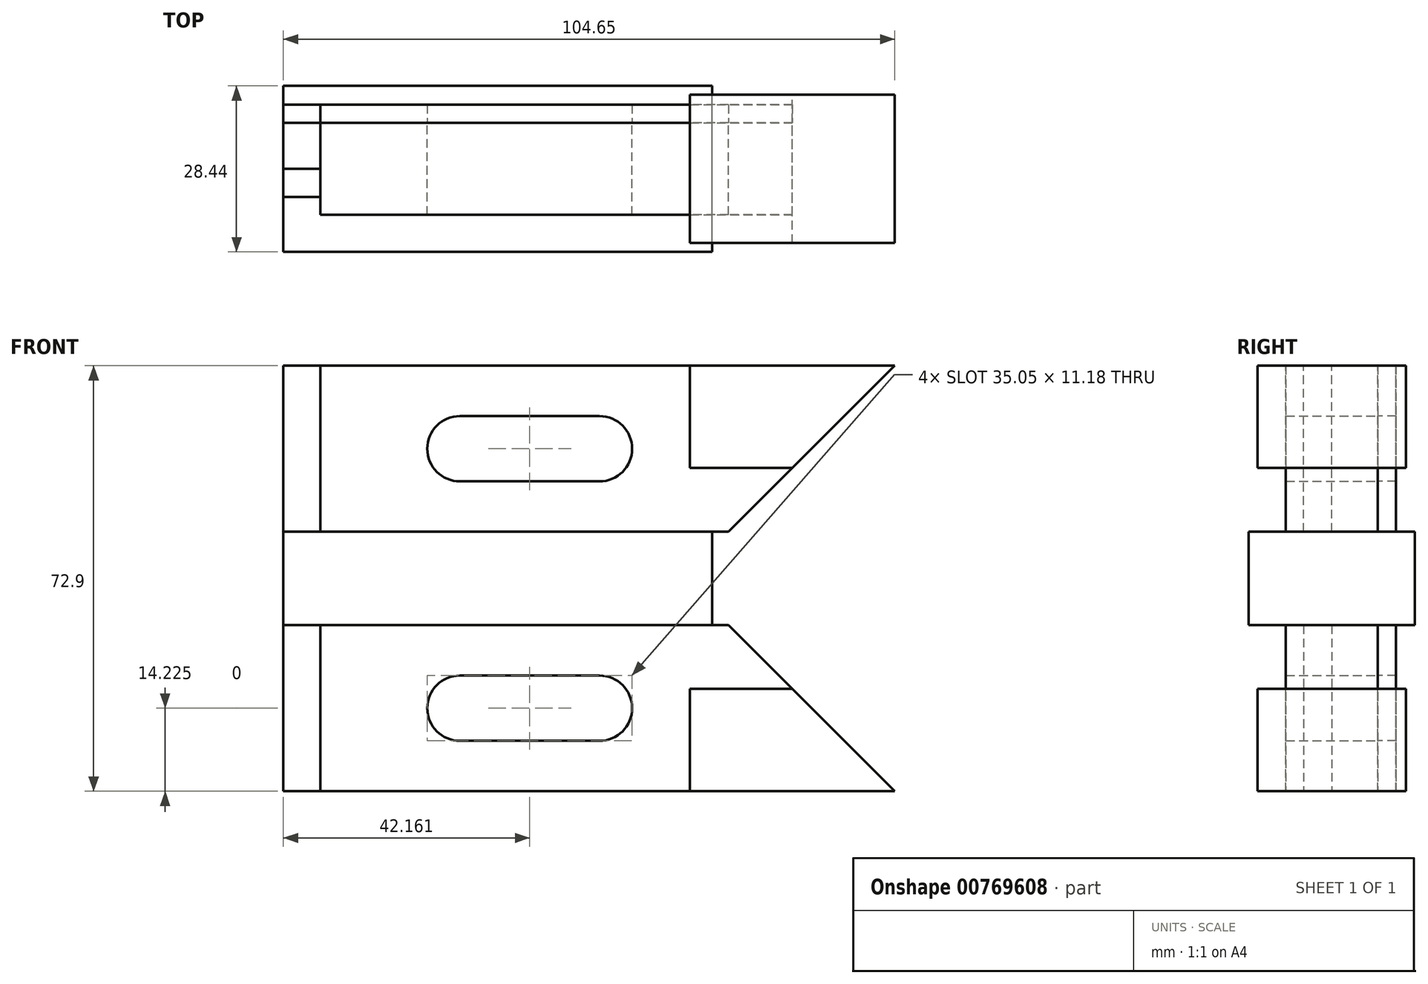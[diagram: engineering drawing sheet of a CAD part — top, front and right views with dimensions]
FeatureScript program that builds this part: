
annotation { "Feature Type Name" : "Feature", "Feature Type Description" : "" }
export const myFeature = defineFeature(function(context is Context, id is Id, definition is map)
    precondition{}
    {
        {
            var Q0;
            Q0=qCreatedBy(makeId("Front.planeOp"),FACE);
            var sketch = newSketch(context, id + "F0", { "sketchPlane" : qUnion([Q0])});
            skLineSegment(sketch, "E0.bottom", {"start": v(36.7, 8) * mm, "end": v(-36.7, 8) * mm});
            skLineSegment(sketch, "E0.top", {"start": v(36.7, -8) * mm, "end": v(-36.7, -8) * mm});
            skLineSegment(sketch, "E0.left", {"start": v(36.7, 8) * mm, "end": v(36.7, -8) * mm});
            skLineSegment(sketch, "E0.right", {"start": v(-36.7, 8) * mm, "end": v(-36.7, -8) * mm});
            skPoint(sketch, "E0.middle", {"position": v(0, 0) * mm});
            skLineSegment(sketch, "E1.bottom", {"start": v(-36.7, 8) * mm, "end": v(36.7, 8) * mm});
            skLineSegment(sketch, "E1.top", {"start": v(-36.7, 36.45) * mm, "end": v(67.94, 36.45) * mm});
            skLineSegment(sketch, "E1.left", {"start": v(-36.7, 8) * mm, "end": v(-36.7, 36.45) * mm});
            skLineSegment(sketch, "E2", {"start": v(-30.35, 8) * mm, "end": v(-30.35, 36.45) * mm});
            skPoint(sketch, "E3.end.orphan", {"position": v(-30.35, 19.55) * mm});
            skPoint(sketch, "E4.start.orphan", {"position": v(-36.7, 75.91) * mm});
            skPoint(sketch, "E5.start.orphan", {"position": v(32.9, 36.45) * mm});
            skLineSegment(sketch, "E6", {"start": v(32.9, 36.45) * mm, "end": v(32.9, 18.92) * mm});
            skPoint(sketch, "E7.end.orphan", {"position": v(32.9, 39.77) * mm});
            skLineSegment(sketch, "E8", {"start": v(32.9, 18.92) * mm, "end": v(50.42, 18.92) * mm});
            skPoint(sketch, "E8.endSnap0", {"position": v(67.94, 22.23) * mm});
            skLineSegment(sketch, "E9", {"start": v(67.95, 36.45) * mm, "end": v(39.5, 8) * mm});
            skPoint(sketch, "E1.right.end.orphan", {"position": v(67.94, 18.92) * mm});
            skPoint(sketch, "E10.orphan", {"position": v(67.95, 8) * mm});
            skLineSegment(sketch, "E11", {"start": v(39.5, 8) * mm, "end": v(36.7, 8) * mm});
            skPoint(sketch, "E12.startSnap0", {"position": v(-30.35, 22.23) * mm});
            skPoint(sketch, "E13.orphan", {"position": v(0, 22.23) * mm});
            skPoint(sketch, "E12.end.orphan", {"position": v(-36.7, 22.23) * mm});
            skCircle(sketch, "E14", {"center": v(-6.48, 22.22) * mm, "radius": 5.59 * mm});
            skCircle(sketch, "E15", {"center": v(17.4, 22.22) * mm, "radius": 5.59 * mm});
            skLineSegment(sketch, "E16.bottom", {"start": v(17.4, 27.81) * mm, "end": v(-6.48, 27.81) * mm});
            skLineSegment(sketch, "E16.top", {"start": v(17.4, 16.64) * mm, "end": v(-6.48, 16.64) * mm});
            skPoint(sketch, "E16.middle", {"position": v(5.46, 22.23) * mm});
            skPoint(sketch, "E17.orphan", {"position": v(-12.07, 27.81) * mm});
            skPoint(sketch, "E18.orphan", {"position": v(-12.07, 16.64) * mm});
            skPoint(sketch, "E19.orphan", {"position": v(22.99, 27.81) * mm});
            skPoint(sketch, "E20.orphan", {"position": v(22.99, 16.64) * mm});
            skPoint(sketch, "E21.trimOffspring.end.orphan", {"position": v(22.99, 22.23) * mm});
            skPoint(sketch, "E22.orphan", {"position": v(-12.07, 22.23) * mm});
            skSolve(sketch);
        }
        {
            var Q0;
            {var subQ3=sQuery(id+"F0.wireOp",EDGE,"E6");Q0=makeQuery(id+"F0.imprint","IMPRINT",FACE,{"disambiguationData":[TD([[makeQuery(id+"F0.imprint","IMPRINT",EDGE,{"derivedFrom":subQ3}),1.0]])]});}
            extrude(context, id + "F1", {"entities" : qUnion([Q0]), "endBound" : BoundingType.SYMMETRIC, "depth" : 25.4 * mm, "offsetDistance" : 25.4 * mm});
        }
        {
            var Q0;
            Q0=makeQuery(id+"F0.imprint","IMPRINT",FACE,{"disambiguationData":[TD([[makeQuery(id+"F0.imprint","IMPRINT",EDGE,{"derivedFrom":sQuery(id+"F0.wireOp",EDGE,"E0.top")}),-1.0]])]});
            extrude(context, id + "F2", {"entities" : qUnion([Q0]), "endBound" : BoundingType.SYMMETRIC, "depth" : 28.45 * mm, "offsetDistance" : 25.4 * mm});
        }
        {
            var Q0;
            {var subQ8=sQuery(id+"F0.wireOp",EDGE,"E2");Q0=makeQuery(id+"F0.imprint","IMPRINT",FACE,{"disambiguationData":[TD([[makeQuery(id+"F0.imprint","IMPRINT",EDGE,{"derivedFrom":subQ8}),-1.0]])]});}
            extrude(context, id + "F3", {"entities" : qUnion([Q0]), "endBound" : BoundingType.SYMMETRIC, "depth" : 15.75 * mm, "offsetDistance" : 25.4 * mm});
        }
        {
            var Q0;
            {var subQ0=sQuery(id+"F0.wireOp",EDGE,"E1.left");Q0=makeQuery(id+"F0.imprint","IMPRINT",FACE,{"disambiguationData":[TD([[makeQuery(id+"F0.imprint","IMPRINT",EDGE,{"derivedFrom":subQ0}),-1.0]])]});}
            extrude(context, id + "F4", {"entities" : qUnion([Q0]), "depth" : 4.83 * mm, "offsetDistance" : 25.4 * mm});
        }
        {
            var Q0;
            {var subQ0=sQuery(id+"F0.wireOp",EDGE,"E1.left");Q0=makeQuery(id+"F0.imprint","IMPRINT",FACE,{"disambiguationData":[TD([[makeQuery(id+"F0.imprint","IMPRINT",EDGE,{"derivedFrom":subQ0}),-1.0]])]});}
            extrude(context, id + "F5", {"entities" : qUnion([Q0]), "oppositeDirection" : true, "depth" : 7.87 * mm, "offsetDistance" : 25.4 * mm});
        }
        {
            var Q0;
            Q0=makeQuery(id+"F5.opExtrude","CAP_FACE",FACE,{"disambiguationData":[OSD([sQuery(id+"F0.wireOp",EDGE,"E1.bottom"),sQuery(id+"F0.wireOp",EDGE,"E1.top"),sQuery(id+"F0.wireOp",EDGE,"E1.left"),sQuery(id+"F0.wireOp",EDGE,"E2")])],"isStart":false});
            var Q1;
            Q1=makeQuery(id+"F3.opExtrude","CAP_FACE",FACE,{"disambiguationData":[OSD([sQuery(id+"F0.wireOp",EDGE,"E1.bottom"),sQuery(id+"F0.wireOp",EDGE,"E1.top"),sQuery(id+"F0.wireOp",EDGE,"E2"),sQuery(id+"F0.wireOp",EDGE,"E6"),sQuery(id+"F0.wireOp",EDGE,"E8"),sQuery(id+"F0.wireOp",EDGE,"E9"),sQuery(id+"F0.wireOp",EDGE,"E11"),sQuery(id+"F0.wireOp",EDGE,"E14"),sQuery(id+"F0.wireOp",EDGE,"E15"),sQuery(id+"F0.wireOp",EDGE,"E16.bottom"),sQuery(id+"F0.wireOp",EDGE,"E16.top")])],"isStart":true});
            extrude(context, id + "F6", {"entities" : qUnion([Q0, Q1]), "depth" : 3.13 * mm, "offsetDistance" : 25.4 * mm});
        }
        {
            var Q0;
            Q0=makeQuery(id+"F2.opExtrude","SWEPT_BODY",BODY,{"disambiguationData":[OSD([sQuery(id+"F0.wireOp",EDGE,"E0.top"),sQuery(id+"F0.wireOp",EDGE,"E0.left"),sQuery(id+"F0.wireOp",EDGE,"E0.right"),sQuery(id+"F0.wireOp",EDGE,"E1.bottom")])]});
            var Q1;
            Q1=makeQuery(id+"F3.opExtrude","SWEPT_BODY",BODY,{"disambiguationData":[OSD([sQuery(id+"F0.wireOp",EDGE,"E1.bottom"),sQuery(id+"F0.wireOp",EDGE,"E1.top"),sQuery(id+"F0.wireOp",EDGE,"E2"),sQuery(id+"F0.wireOp",EDGE,"E6"),sQuery(id+"F0.wireOp",EDGE,"E8"),sQuery(id+"F0.wireOp",EDGE,"E9"),sQuery(id+"F0.wireOp",EDGE,"E11"),sQuery(id+"F0.wireOp",EDGE,"E14"),sQuery(id+"F0.wireOp",EDGE,"E15"),sQuery(id+"F0.wireOp",EDGE,"E16.bottom"),sQuery(id+"F0.wireOp",EDGE,"E16.top")])]});
            var Q2;
            Q2=makeQuery(id+"F4.opExtrude","SWEPT_BODY",BODY,{"disambiguationData":[OSD([sQuery(id+"F0.wireOp",EDGE,"E1.bottom"),sQuery(id+"F0.wireOp",EDGE,"E1.top"),sQuery(id+"F0.wireOp",EDGE,"E1.left"),sQuery(id+"F0.wireOp",EDGE,"E2")])]});
            var Q3;
            Q3=makeQuery(id+"F5.opExtrude","SWEPT_BODY",BODY,{"disambiguationData":[OSD([sQuery(id+"F0.wireOp",EDGE,"E1.bottom"),sQuery(id+"F0.wireOp",EDGE,"E1.top"),sQuery(id+"F0.wireOp",EDGE,"E1.left"),sQuery(id+"F0.wireOp",EDGE,"E2")])]});
            var Q4;
            Q4=makeQuery(id+"F6.opExtrude","SWEPT_BODY",BODY,{"disambiguationData":[OSD([sQuery(id+"F0.wireOp",EDGE,"E1.bottom"),sQuery(id+"F0.wireOp",EDGE,"E1.top"),sQuery(id+"F0.wireOp",EDGE,"E1.left"),sQuery(id+"F0.wireOp",EDGE,"E2")])]});
            var Q5;
            Q5=makeQuery(id+"F1.opExtrude","SWEPT_BODY",BODY,{"disambiguationData":[OSD([sQuery(id+"F0.wireOp",EDGE,"E1.top"),sQuery(id+"F0.wireOp",EDGE,"E6"),sQuery(id+"F0.wireOp",EDGE,"E8"),sQuery(id+"F0.wireOp",EDGE,"E9")])]});
            var Q6;
            Q6=makeQuery(id+"F6.opExtrude","SWEPT_BODY",BODY,{"disambiguationData":[OSD([sQuery(id+"F0.wireOp",EDGE,"E1.bottom"),sQuery(id+"F0.wireOp",EDGE,"E1.top"),sQuery(id+"F0.wireOp",EDGE,"E2"),sQuery(id+"F0.wireOp",EDGE,"E6"),sQuery(id+"F0.wireOp",EDGE,"E8"),sQuery(id+"F0.wireOp",EDGE,"E9"),sQuery(id+"F0.wireOp",EDGE,"E11"),sQuery(id+"F0.wireOp",EDGE,"E14"),sQuery(id+"F0.wireOp",EDGE,"E15"),sQuery(id+"F0.wireOp",EDGE,"E16.bottom"),sQuery(id+"F0.wireOp",EDGE,"E16.top")])]});
            var Q7;
            Q7=qCreatedBy(makeId("Top.planeOp"),FACE);
            mirror(context, id + "F7", {"entities" : qUnion([Q0, Q1, Q2, Q3, Q4, Q5, Q6]), "mirrorPlane" : qUnion([Q7])});
        }
    });
